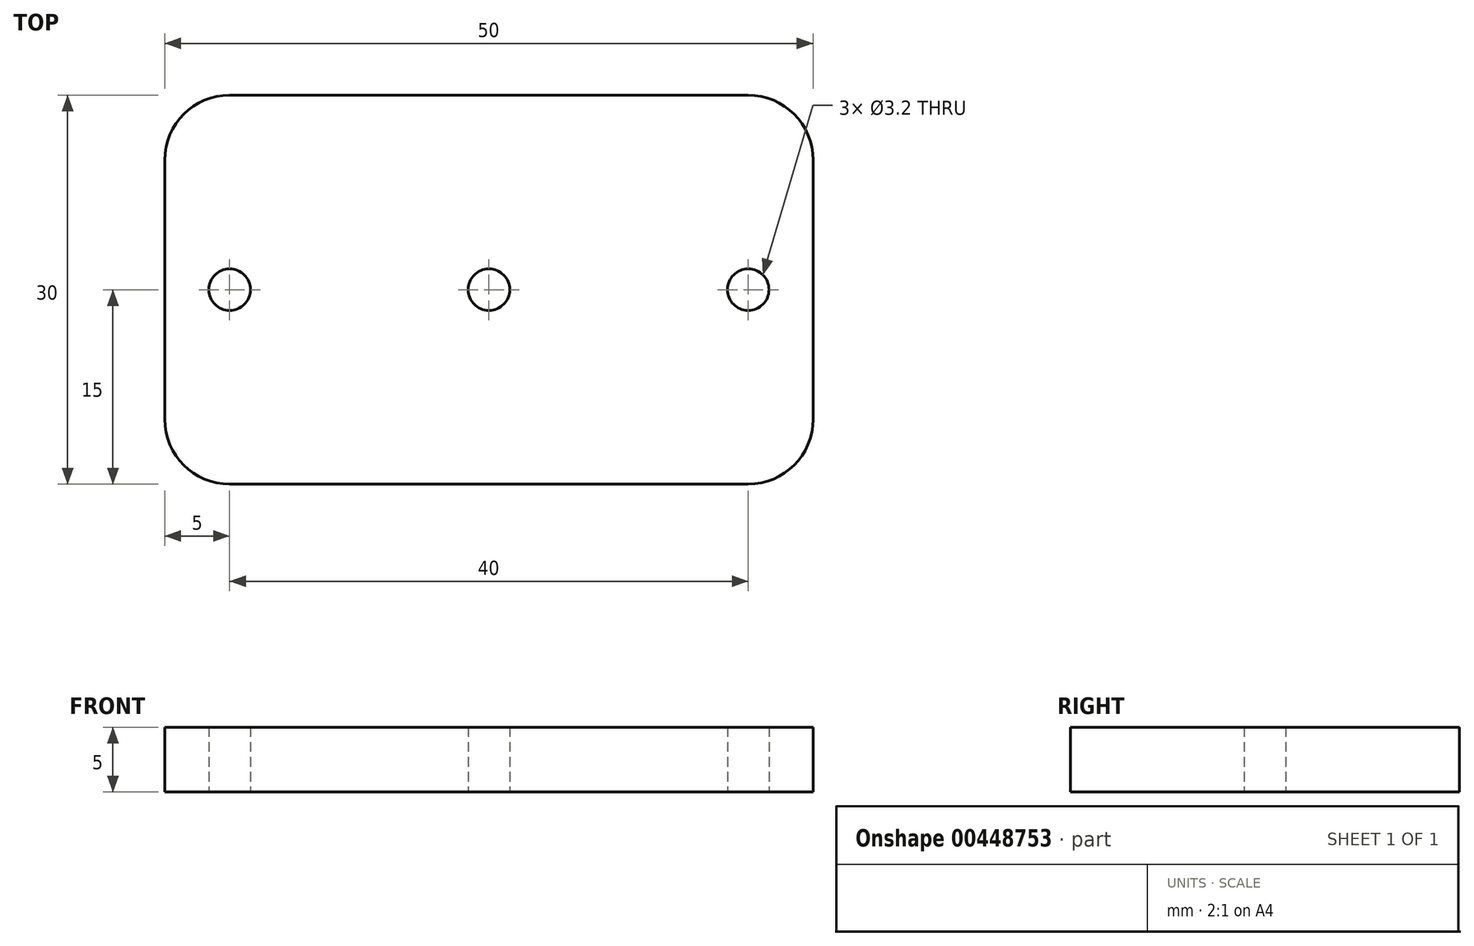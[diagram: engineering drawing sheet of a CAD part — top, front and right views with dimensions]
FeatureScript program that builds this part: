
annotation { "Feature Type Name" : "Feature", "Feature Type Description" : "" }
export const myFeature = defineFeature(function(context is Context, id is Id, definition is map)
    precondition{}
    {
        {
            var Q0;
            Q0=qCreatedBy(makeId("Top.planeOp"),FACE);
            var sketch = newSketch(context, id + "F0", { "sketchPlane" : qUnion([Q0])});
            skLineSegment(sketch, "E0.bottom", {"start": v(20, 15) * mm, "end": v(-20, 15) * mm});
            skLineSegment(sketch, "E0.top", {"start": v(20, -15) * mm, "end": v(-20, -15) * mm});
            skLineSegment(sketch, "E0.left", {"start": v(25, 10) * mm, "end": v(25, -10) * mm});
            skLineSegment(sketch, "E0.right", {"start": v(-25, 10) * mm, "end": v(-25, -10) * mm});
            skPoint(sketch, "E0.middle", {"position": v(0, 0) * mm});
            skLineSegment(sketch, "E1", {"start": v(-10, 15) * mm, "end": v(-10, -15) * mm, "construction": true});
            skLineSegment(sketch, "E2", {"start": v(10, 15) * mm, "end": v(10, -15) * mm, "construction": true});
            skLineSegment(sketch, "E3", {"start": v(-15, 15) * mm, "end": v(-15, -15) * mm, "construction": true});
            skCircle(sketch, "E4", {"center": v(-20, 0) * mm, "radius": 1.6 * mm});
            skLineSegment(sketch, "E5", {"start": v(0, 15) * mm, "end": v(0, -15) * mm, "construction": true});
            skCircle(sketch, "E6.MirrorC", {"center": v(20, 0) * mm, "radius": 1.6 * mm});
            skCircle(sketch, "E7", {"center": v(0, 0) * mm, "radius": 1.6 * mm});
            skPoint(sketch, "E8.visualSharp", {"position": v(-25, 15) * mm});
            skArc(sketch, "E8.filletArc", {"start": v(-20, 15) * mm, "mid": v(-23.54, 13.54) * mm, "end": v(-25, 10) * mm});
            skPoint(sketch, "E9.visualSharp", {"position": v(25, 15) * mm});
            skArc(sketch, "E9.filletArc", {"start": v(25, 10) * mm, "mid": v(23.54, 13.54) * mm, "end": v(20, 15) * mm});
            skPoint(sketch, "E10.visualSharp", {"position": v(25, -15) * mm});
            skArc(sketch, "E10.filletArc", {"start": v(20, -15) * mm, "mid": v(23.54, -13.54) * mm, "end": v(25, -10) * mm});
            skPoint(sketch, "E11.visualSharp", {"position": v(-25, -15) * mm});
            skArc(sketch, "E11.filletArc", {"start": v(-25, -10) * mm, "mid": v(-23.54, -13.54) * mm, "end": v(-20, -15) * mm});
            skSolve(sketch);
        }
        {
            var Q0;
            Q0=qSketchRegion(id+"F0",true);
            extrude(context, id + "F1", {"entities" : qUnion([Q0]), "depth" : 5 * mm});
        }
    });
